# Revit family: IS_ConnectAir_E0694_BIM_DE
name_source: partatom
category: Plumbing Fixtures
revit_build: Autodesk Revit MEP 2016 (Build: 20161004_0715(x64)
units: mm (PartAtom-declared; Revit-internal decimal feet)

## family parameters
Always vertical = Yes
Cut with Voids When Loaded = No
OmniClass Number = 23.45.05.14.14
OmniClass Title = Sinks/Lavatories
Part Type = Normal
Room Calculation Point = No
Round Connector Dimension = Use Diameter
Shared = No
Work Plane-Based = No

## types (2) — shared parameters
Accessories = www.idealspec.co.uk
AreaUnits = millimeters
Assembly Code = C1030200
AssetType = Fixed
BIMObjectName = ISI_IdealStandard_WashbasinTaps_ConnectAir_E0694
Brand = Ideal Standard
Color = White
ConnectionType = Plumbing
Description = C.AIR ARC BASIN 60X46 WHITE
DurationUnit = year
Features = C.AIR ARC BASIN 60X46 WHITE
Finish = White
Help = www.idealstandard.de
IfcExportAs = IfcValveType
IfcExportType = BASIN MIXER
InstallationInstructions = www.idealstandard.de
LinearUnits = millimeters
MainColor = White
MaintenanceInformation = www.idealstandard.de
Manufacturer = www.idealstandard.de
ManufacturerURL = www.idealstandard.de
ModelNumber = E069401
ModelReference = C.AIR ARC BASIN 60X46 WHITE
Name = WashbasinTaps_ConnectAir_E0694_ISI
NettWeight = 14,10 KG
NominalDepth = 600 mm
NominalHeight = 160 mm
NominalLength = 600 mm
NominalWidth = 460 mm
ProductInformation = www.idealstandard.de
Shape = Sculptured
Size = 160 x 600 x 460 mm
Space = Internal
SpareParts = www.idealstandard.de
URL = www.idealstandard.de
Uniclass2015Code = Pr_40_20_87_98
Uniclass2015Title = Washbasin taps
Uniclass2015Version = Products v1.1
zero-valued in all types: Cost, DrainSize

## per-type parameters (varying)
| type | BarCode | Model |
| E069401 CONNECT AIR ARC washbasin 600x460mm, 1 taphole, with overflow | 5017830526032 | E069401 |
| E0694MA CONNECT AIR ARC washbasin 600x460mm, 1 taphole, with overflow | 5017830528081 | E0694MA |

## geometry (parser evidence)
native form markers: Blend x4
no freeform markers — native parametric forms only
